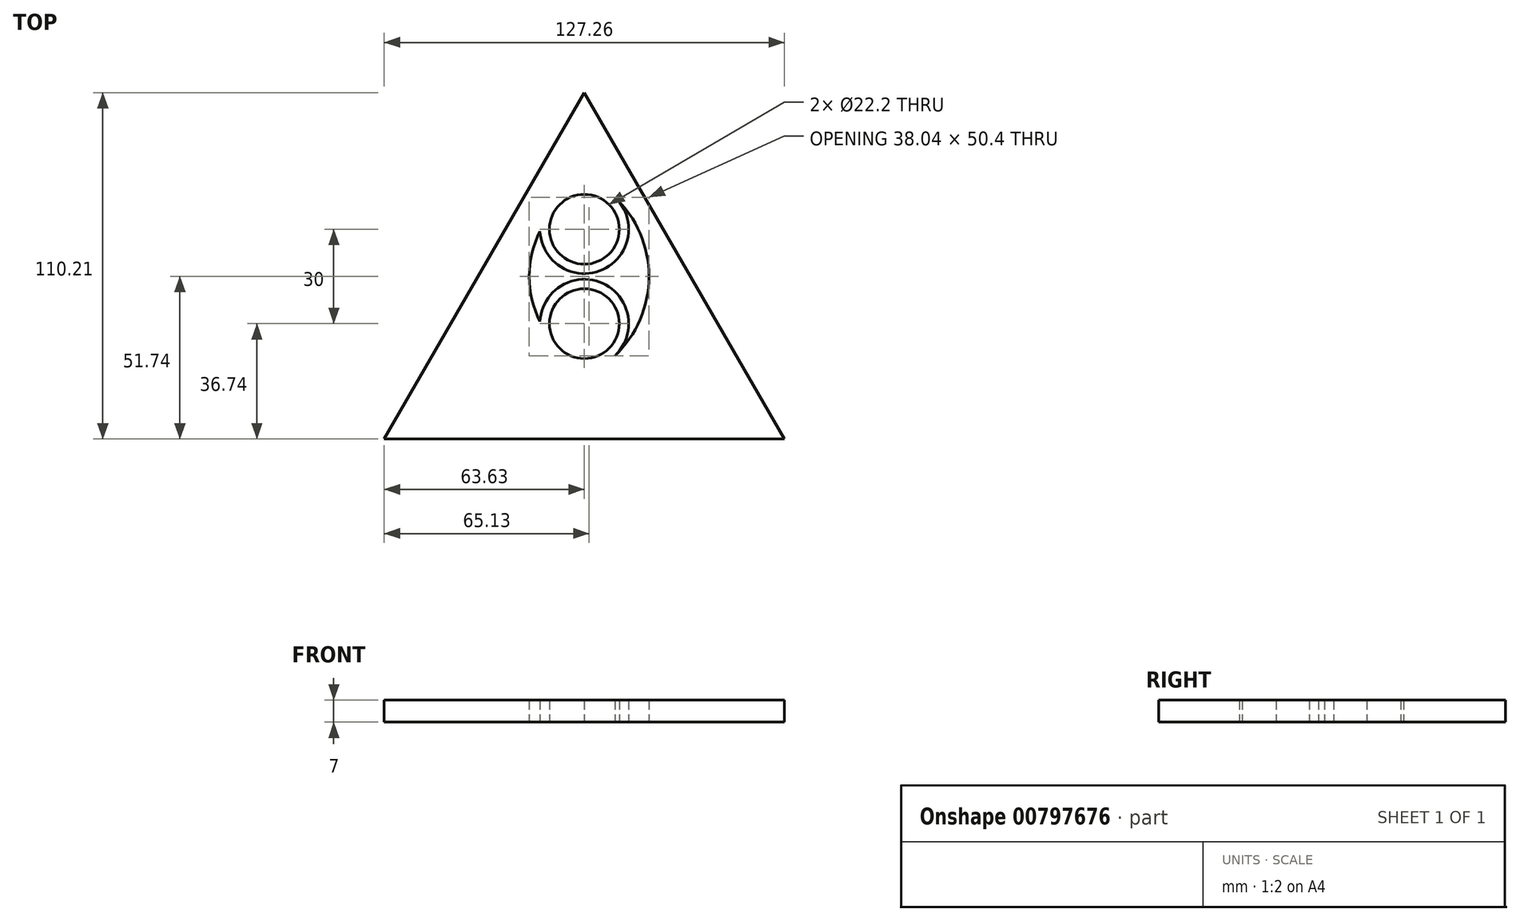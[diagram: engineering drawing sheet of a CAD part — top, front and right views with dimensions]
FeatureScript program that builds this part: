
annotation { "Feature Type Name" : "Feature", "Feature Type Description" : "" }
export const myFeature = defineFeature(function(context is Context, id is Id, definition is map)
    precondition{}
    {
        {
            var Q0;
            Q0=qCreatedBy(makeId("Top.planeOp"),FACE);
            var sketch = newSketch(context, id + "F0", { "sketchPlane" : qUnion([Q0])});
            skCircle(sketch, "E0", {"center": v(0, 0) * mm, "radius": 11.1 * mm});
            skCircle(sketch, "E1.cCircle", {"center": v(0, 0) * mm, "radius": 15 * mm, "construction": true});
            skLineSegment(sketch, "E1.0", {"start": v(25.98, -15) * mm, "end": v(-25.98, -15) * mm, "construction": true});
            skLineSegment(sketch, "E1.1", {"start": v(-25.98, -15) * mm, "end": v(0, 30) * mm, "construction": true});
            skLineSegment(sketch, "E1.2", {"start": v(0, 30) * mm, "end": v(25.98, -15) * mm, "construction": true});
            skPoint(sketch, "E1.0.midPoint", {"position": v(0, -15) * mm});
            skCircle(sketch, "E2", {"center": v(0, 30) * mm, "radius": 11.1 * mm});
            skLineSegment(sketch, "E3", {"start": v(-13, 7.5) * mm, "end": v(13, 7.5) * mm, "construction": true});
            skLineSegment(sketch, "E4", {"start": v(0, -15) * mm, "end": v(0, 0) * mm, "construction": true});
            skLineSegment(sketch, "E5", {"start": v(13, 7.5) * mm, "end": v(0, -15) * mm, "construction": true});
            skLineSegment(sketch, "E6", {"start": v(-13, 7.5) * mm, "end": v(0, -15) * mm, "construction": true});
            skCircle(sketch, "E7.cCircle", {"center": v(0, 0) * mm, "radius": 36.74 * mm, "construction": true});
            skLineSegment(sketch, "E7.0", {"start": v(63.63, -36.74) * mm, "end": v(-63.63, -36.74) * mm});
            skLineSegment(sketch, "E7.1", {"start": v(-63.63, -36.74) * mm, "end": v(0, 73.47) * mm});
            skLineSegment(sketch, "E7.2", {"start": v(0, 73.47) * mm, "end": v(63.63, -36.74) * mm});
            skPoint(sketch, "E7.0.midPoint", {"position": v(0, -36.74) * mm});
            skCircle(sketch, "E8", {"center": v(0, 30) * mm, "radius": 14.1 * mm});
            skCircle(sketch, "E9", {"center": v(0, 0) * mm, "radius": 14.1 * mm});
            skLineSegment(sketch, "E10", {"start": v(0, 30) * mm, "end": v(0, 0) * mm, "construction": true});
            skLineSegment(sketch, "E11", {"start": v(0, 15) * mm, "end": v(-14.31, 15) * mm, "construction": true});
            skArc(sketch, "E12", {"start": v(9.73, 40.2) * mm, "mid": v(20.52, 15) * mm, "end": v(9.73, -10.2) * mm});
            skArc(sketch, "E13", {"start": v(14.09, 29.38) * mm, "mid": v(17.52, 15) * mm, "end": v(14.09, 0.62) * mm});
            skArc(sketch, "E14.MirrorCS", {"start": v(-14.09, 29.38) * mm, "mid": v(-17.52, 15) * mm, "end": v(-14.09, 0.62) * mm});
            skArc(sketch, "E15.MirrorCS", {"start": v(-9.73, 40.2) * mm, "mid": v(-20.52, 15) * mm, "end": v(-9.73, -10.2) * mm});
            skSolve(sketch);
        }
        {
            var Q0;
            Q0=makeQuery(id+"F0.imprint","IMPRINT",FACE,{"disambiguationData":[TD([[makeQuery(id+"F0.imprint","IMPRINT",EDGE,{"derivedFrom":sQuery(id+"F0.wireOp",EDGE,"E2")}),-1.0]])]});
            var Q1;
            {var subQ0=sQuery(id+"F0.wireOp",EDGE,"E12");Q1=makeQuery(id+"F0.imprint","IMPRINT",FACE,{"disambiguationData":[TD([[makeQuery(id+"F0.imprint","IMPRINT",EDGE,{"derivedFrom":subQ0}),-1.0]])]});}
            var Q2;
            Q2=makeQuery(id+"F0.imprint","IMPRINT",FACE,{"disambiguationData":[TD([[makeQuery(id+"F0.imprint","IMPRINT",EDGE,{"derivedFrom":sQuery(id+"F0.wireOp",EDGE,"E0")}),-1.0]])]});
            var Q3;
            {var subQ0=sQuery(id+"F0.wireOp",EDGE,"E14.MirrorCS");Q3=makeQuery(id+"F0.imprint","IMPRINT",FACE,{"disambiguationData":[TD([[makeQuery(id+"F0.imprint","IMPRINT",EDGE,{"derivedFrom":subQ0}),-1.0]])]});}
            extrude(context, id + "F1", {"entities" : qUnion([Q0, Q1, Q2, Q3]), "depth" : 7 * mm, "offsetDistance" : 25 * mm});
        }
    });
